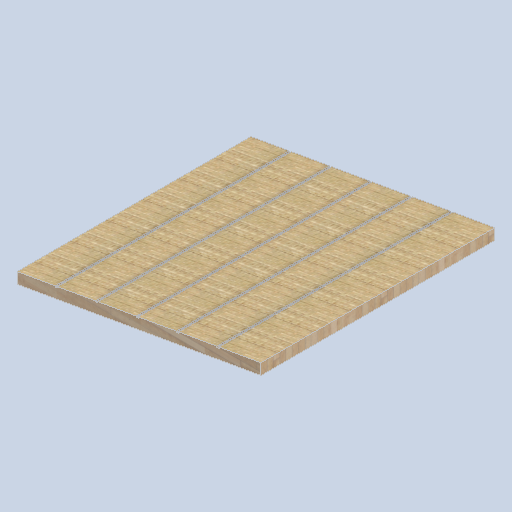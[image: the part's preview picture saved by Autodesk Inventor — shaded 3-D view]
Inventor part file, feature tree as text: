
AUTODESK INVENTOR PART (.ipt)
format: ipt  version: 2024.2 (Build 282272000, 272)  size: 251,392 bytes
history: native  units: in
note: dims shown in document units (in); Inventor stores cm internally (conversion verified against a paired STEP export)
features: sketch x4, other x3, plane x3
ambient origin geometry x8: Origin, YZ Plane, XZ Plane, XY Plane, X Axis, Y Axis, Z Axis, Center Point
bodies: Solid1 (feature_tree)
feature tree (10):
  other  "eave_panel_side.ipt"
  other  "Solid1::eave_panel_side.ipt"
  other  "TaggingFeature1"
  sketch  "Sketch1"  dims[d0=0.3937in]
  sketch  "Sketch2"
  sketch  "Sketch3"
  sketch  "Sketch4"
  plane  "Work Plane1"
  plane  "Work Plane2"
  plane  "Work Plane3"
